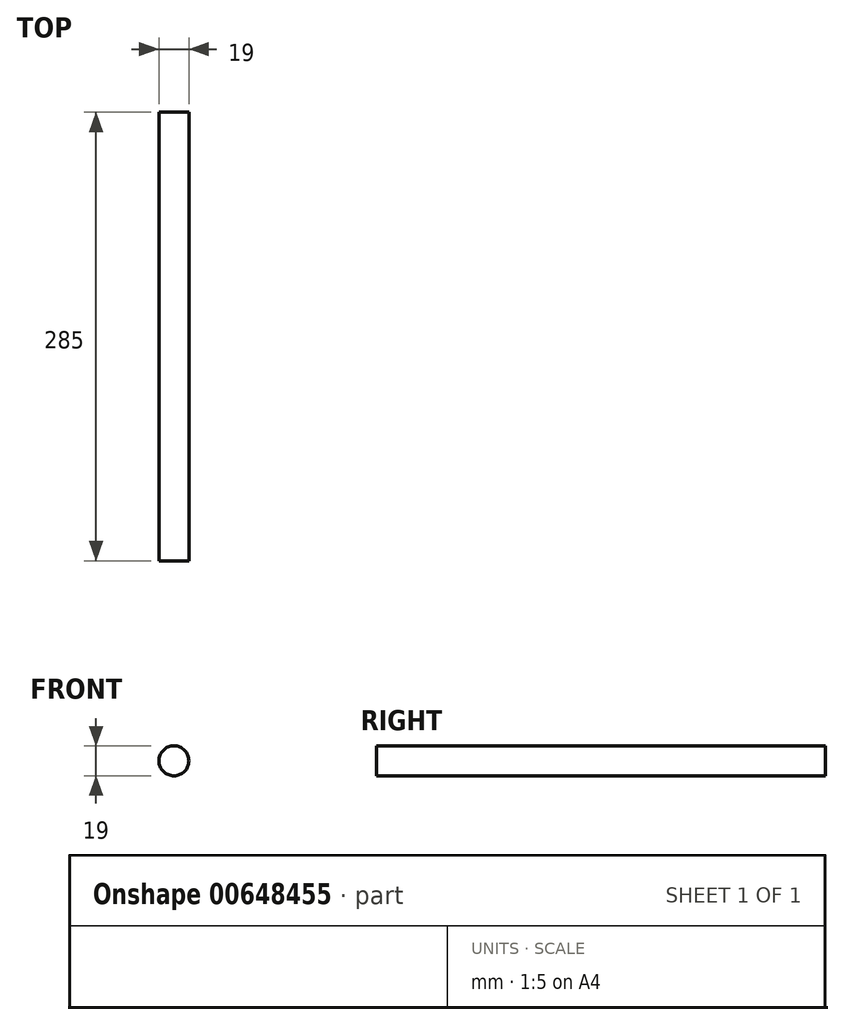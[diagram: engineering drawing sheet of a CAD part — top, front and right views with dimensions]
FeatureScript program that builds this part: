
annotation { "Feature Type Name" : "Feature", "Feature Type Description" : "" }
export const myFeature = defineFeature(function(context is Context, id is Id, definition is map)
    precondition{}
    {
        {
            var Q0;
            Q0=qCreatedBy(makeId("Front.planeOp"),FACE);
            var sketch = newSketch(context, id + "F0", { "sketchPlane" : qUnion([Q0])});
            skCircle(sketch, "E0", {"center": v(0, 0) * mm, "radius": 9.5 * mm});
            skSolve(sketch);
        }
        {
            var Q0;
            Q0=makeQuery(id+"F0.imprint","IMPRINT",FACE,{"disambiguationData":[TD([[makeQuery(id+"F0.imprint","IMPRINT",EDGE,{"derivedFrom":sQuery(id+"F0.wireOp",EDGE,"E0")}),1.0]])]});
            var Q1;
            Q1=sQuery(id+"F0.wireOp",EDGE,"E0");
            extrude(context, id + "F1", {"entities" : qUnion([Q0]), "surfaceEntities" : qUnion([Q1]), "oppositeDirection" : true, "depth" : 285 * mm, "offsetDistance" : 25 * mm});
        }
    });
